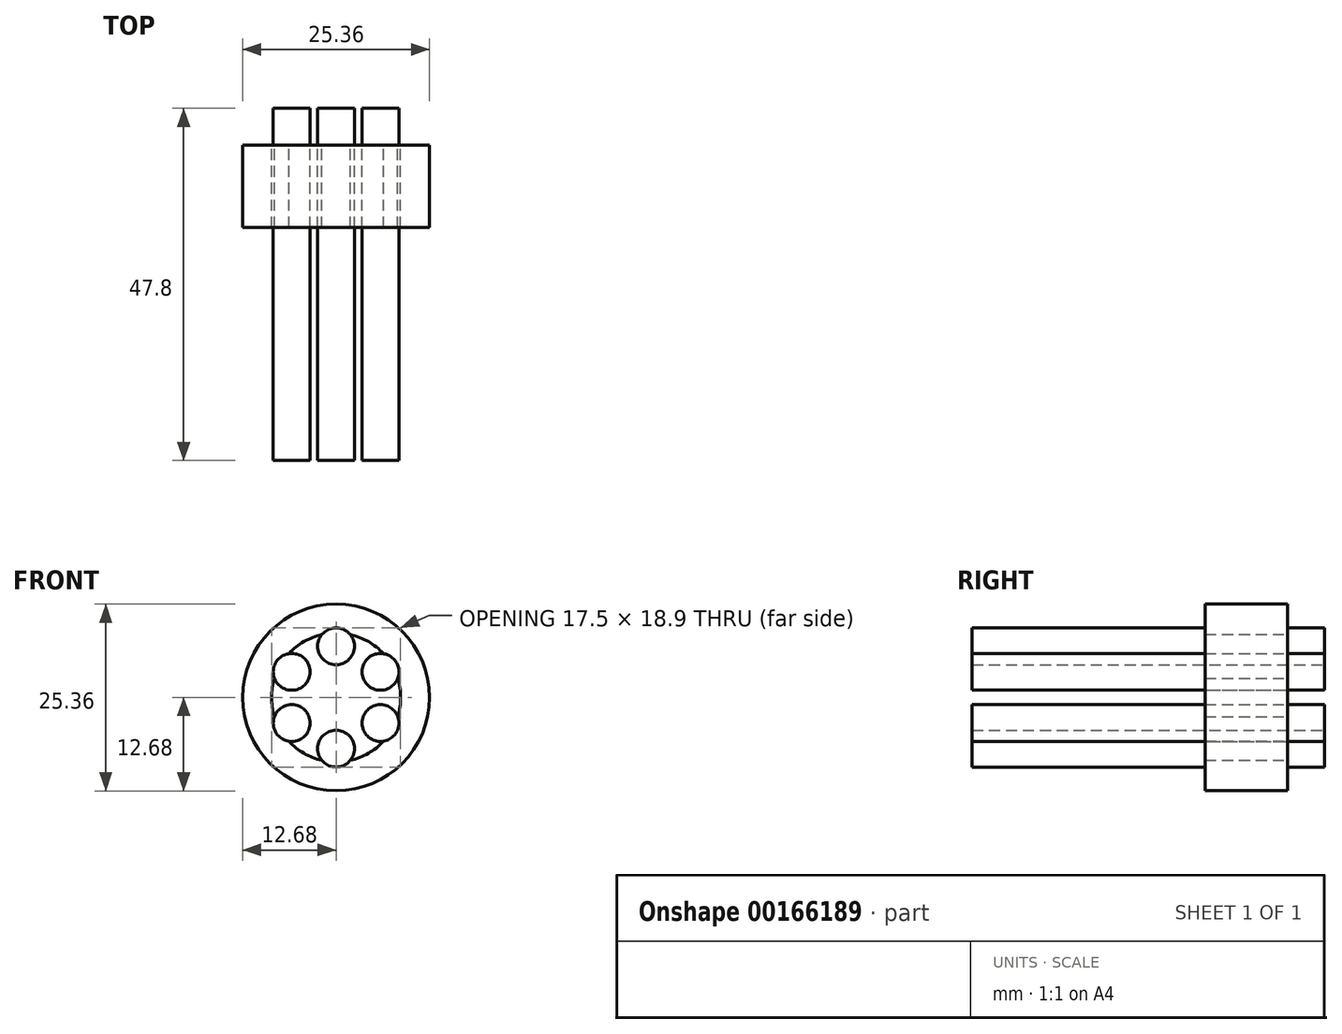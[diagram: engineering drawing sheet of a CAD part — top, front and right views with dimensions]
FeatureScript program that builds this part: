
annotation { "Feature Type Name" : "Feature", "Feature Type Description" : "" }
export const myFeature = defineFeature(function(context is Context, id is Id, definition is map)
    precondition{}
    {
        {
            var Q0;
            Q0=qCreatedBy(makeId("Front.planeOp"),FACE);
            var sketch = newSketch(context, id + "F0", { "sketchPlane" : qUnion([Q0])});
            skCircle(sketch, "E0.cCircle", {"center": v(0, 0) * mm, "radius": 6.95 * mm, "construction": true});
            skLineSegment(sketch, "E0.0", {"start": v(0, 6.95) * mm, "end": v(6.02, 3.48) * mm, "construction": true});
            skLineSegment(sketch, "E0.1", {"start": v(6.02, 3.48) * mm, "end": v(6.02, -3.47) * mm, "construction": true});
            skLineSegment(sketch, "E0.2", {"start": v(6.02, -3.47) * mm, "end": v(0, -6.95) * mm, "construction": true});
            skLineSegment(sketch, "E0.3", {"start": v(0, -6.95) * mm, "end": v(-6.02, -3.48) * mm, "construction": true});
            skLineSegment(sketch, "E0.4", {"start": v(-6.02, -3.48) * mm, "end": v(-6.02, 3.47) * mm, "construction": true});
            skLineSegment(sketch, "E0.5", {"start": v(-6.02, 3.47) * mm, "end": v(0, 6.95) * mm, "construction": true});
            skCircle(sketch, "E1", {"center": v(0, 6.95) * mm, "radius": 2.5 * mm});
            skCircle(sketch, "E2.1.0", {"center": v(-6.02, 3.47) * mm, "radius": 2.5 * mm});
            skCircle(sketch, "E2.2.0", {"center": v(-6.02, -3.48) * mm, "radius": 2.5 * mm});
            skCircle(sketch, "E2.3.0", {"center": v(0, -6.95) * mm, "radius": 2.5 * mm});
            skCircle(sketch, "E2.4.0", {"center": v(6.02, -3.47) * mm, "radius": 2.5 * mm});
            skCircle(sketch, "E2.5.0", {"center": v(6.02, 3.48) * mm, "radius": 2.5 * mm});
            skSolve(sketch);
        }
        {
            var Q0;
            Q0 = qSketchRegion(id + "F0", true);
            extrude(context, id + "F1", {"entities" : qUnion([Q0]), "depth" : 47.8 * mm});
        }
        {
            var Q0;
            Q0=qCreatedBy(makeId("Front.planeOp"),FACE);
            cPlane(context, id + "F2", {"entities" : qUnion([Q0]), "cplaneType" : CPlaneType.OFFSET, "offset" : 5 * mm, "width" : 150 * mm, "height" : 150 * mm});
        }
        {
            var Q0;
            Q0=qCreatedBy(id+"F2.planeOp",FACE);
            var sketch = newSketch(context, id + "F3", { "sketchPlane" : qUnion([Q0])});
            skCircle(sketch, "E3", {"center": v(0, 0) * mm, "radius": 12.67 * mm});
            skCircle(sketch, "E4", {"center": v(0, 0) * mm, "radius": 8.75 * mm});
            skSolve(sketch);
        }
        {
            var Q0;
            Q0 = qSketchRegion(id + "F3", true);
            extrude(context, id + "F4", {"entities" : qUnion([Q0]), "operationType" : NewBodyOperationType.ADD, "depth" : 11.2 * mm});
        }
    });
